# Revit family: Door-Hardware_Exit-Device_Hager_4600-Trim
name_source: partatom
category: Specialty Equipment
units: mm (PartAtom-declared; Revit-internal decimal feet)

## family parameters
Always vertical = No
Classification Number = 23.30.40.31
Cut with Voids When Loaded = No
Enable Cutting in Views = No
Maintain Annotation Orientation = No
Part Type = Normal
Room Calculation Point = No
Round Connector Dimension = Use Diameter
Shared = Yes
Work Plane-Based = Yes

## types (4) — shared parameters
Assembly Code = C1020410
Default Elevation = 0' - 0"
Keynote = 087100
Manufacturer = Hager Companies
Manufacturer Fax = 800-782-0149
Manufacturer Website = http://www.hagerco.com
Operating Temperature Range = Interior - Exterior
Product Data = http://www.arcat.com
Revision = R1_2015-10
Sales Information = http://www.hagerco.com
Specification = http://www.arcat.com
Standards Conformance = Grade 1
URL = http://www.hagerco.com
zero-valued in all types: Expected Lifespan (Years), Maintenance Schedule (Months), Warranty Duration (Years)

## per-type parameters (varying)
| type | Cylinder | Description | Function Description | Function Type | Keying Function | Model | Night Latch |
| Cylinder Escutcheon | Yes | Hager Grade 1 Exit Device Trim - 4600 Series 46CExxx as Specified | Key unlocks and locks Lever | Function 08 | Keyed | 46CExxx | No |
| Blank Escutcheon | No | Hager Grade 1 Exit Device Trim - 4600 Series 46BExxx as Specified | Always Operable | Function 14 | Not Keyed | 46BExxx | No |
| Night Latch Escutcheon | No | Hager Grade 1 Exit Device Trim - 4600 Series 46NLxxx as Specified | Key retracts latchbolt | Function 03 | Keyed | 46NLxxx | Yes |
| Dummy Escutcheon | No | Hager Grade 1 Exit Device Trim - 4600 Series 46DTxxx as Specified | Dummy | Function 02 | Not Keyed | 46DTxxx | No |

## geometry (parser evidence)
native form markers: Blend x6, Sweep x4
no freeform markers — native parametric forms only
